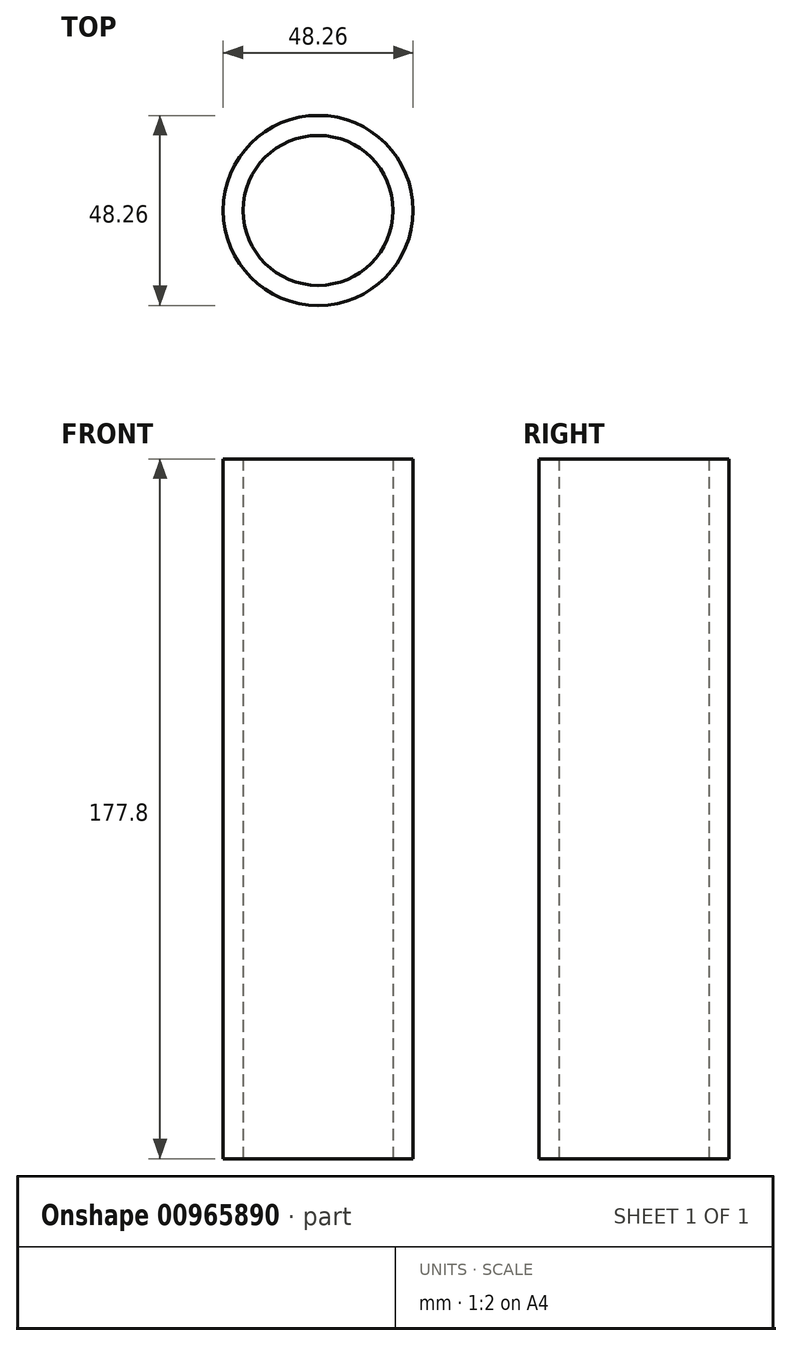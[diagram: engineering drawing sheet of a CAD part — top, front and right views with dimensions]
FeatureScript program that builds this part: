
annotation { "Feature Type Name" : "Feature", "Feature Type Description" : "" }
export const myFeature = defineFeature(function(context is Context, id is Id, definition is map)
    precondition{}
    {
        {
            var Q0;
            Q0=qCreatedBy(makeId("Top.planeOp"),FACE);
            var sketch = newSketch(context, id + "F0", { "sketchPlane" : qUnion([Q0])});
            skCircle(sketch, "E0", {"center": v(0, 0) * mm, "radius": 19.05 * mm});
            skCircle(sketch, "E1", {"center": v(0, 0) * mm, "radius": 24.13 * mm});
            skSolve(sketch);
        }
        {
            var Q0;
            Q0=makeQuery(id+"F0.imprint","IMPRINT",FACE,{"disambiguationData":[TD([[makeQuery(id+"F0.imprint","IMPRINT",EDGE,{"derivedFrom":sQuery(id+"F0.wireOp",EDGE,"E0")}),-1.0]])]});
            extrude(context, id + "F1", {"entities" : qUnion([Q0]), "depth" : 177.8 * mm, "offsetDistance" : 25.4 * mm});
        }
    });
